# Revit family: Sanitary_Showers_hansgrohe_27353400-Crometta-Shower-set-Vario-with_
name_source: partatom
category: Plumbing Fixtures
revit_build: Autodesk Revit 2015 (Build: 20140903_1530(x64)
units: mm (PartAtom-declared; Revit-internal decimal feet)

## types (1)
- Default
    BIMobject category = Showers
    BIMobject category code = sanitary-showers
    BIMobject main category = Sanitary
    BIMobject main category code = sanitary
    Brand url = http://www.hansgrohe-int.com
    Design country = Germany
    Edition number = 1
    GTIN code = https://4011097815718
    IFC Classification = Sanitary Terminal
    Manufacturer country = Germany
    Manufacturer name = hansgrohe
    Material main = Chrome
    Product Guid = 2cc4d81d-0363-431d-a5e8-a4385c06eee1
    Product SKU = 27353400
    Product data url = https://bimobject.com
    Product family = Crometta
    Product group = Wall bar sets
    Product name = 27353400 Crometta Shower set Vario with shower bar 72 cm
    QR code = http://bimobject.com

## geometry (parser evidence)
native form markers: Sweep x2
no freeform markers — native parametric forms only
